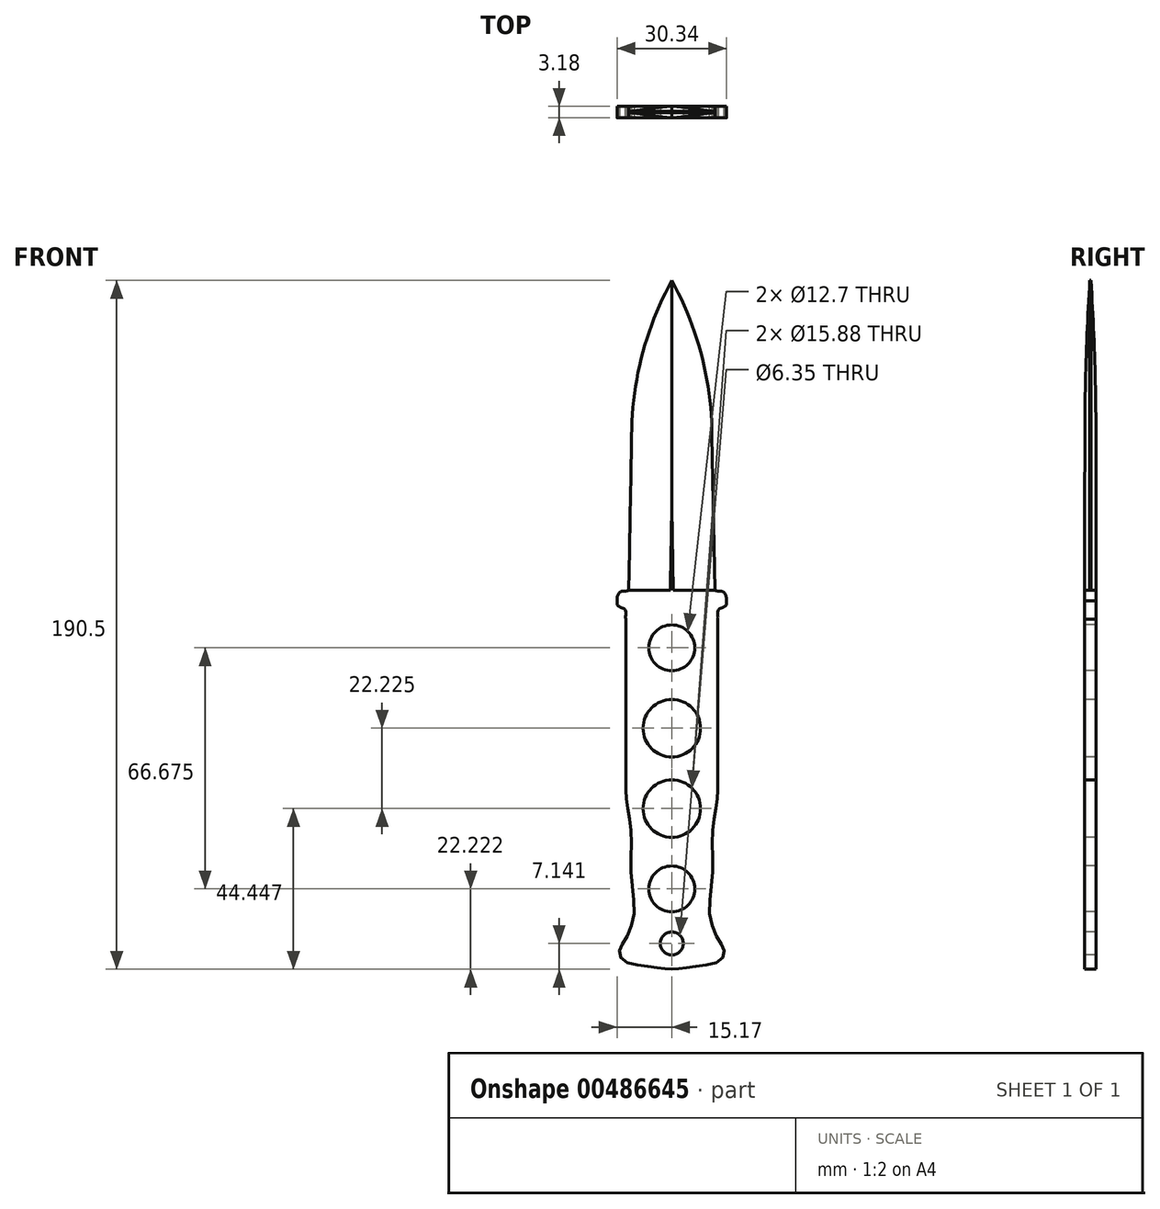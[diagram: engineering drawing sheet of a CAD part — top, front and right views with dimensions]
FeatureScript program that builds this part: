
annotation { "Feature Type Name" : "Feature", "Feature Type Description" : "" }
export const myFeature = defineFeature(function(context is Context, id is Id, definition is map)
    precondition{}
    {
        {
            var Q0;
            Q0=qCreatedBy(makeId("Front.planeOp"),FACE);
            var sketch = newSketch(context, id + "F0", { "sketchPlane" : qUnion([Q0])});
            skLineSegment(sketch, "E0", {"start": v(11.9, -41.46) * mm, "end": v(11.11, 1.4) * mm});
            skArc(sketch, "E1", {"start": v(11.11, 1.4) * mm, "mid": v(8.24, 23.53) * mm, "end": v(0, 44.27) * mm});
            skLineSegment(sketch, "E2", {"start": v(-11.9, -41.46) * mm, "end": v(-11.11, 1.4) * mm});
            skArc(sketch, "E3", {"start": v(0, 44.27) * mm, "mid": v(-8.24, 23.53) * mm, "end": v(-11.11, 1.4) * mm});
            skFitSpline(sketch, "E4", {"points": [v(11.9, -41.46) * mm, v(12.83, -41.64) * mm, v(14.42, -41.94) * mm, v(15.12, -43.63) * mm, v(15.12, -44.27) * mm]});
            skFitSpline(sketch, "E5", {"points": [v(-11.9, -41.46) * mm, v(-12.83, -41.64) * mm, v(-14.42, -41.94) * mm, v(-15.12, -43.63) * mm, v(-15.12, -44.27) * mm]});
            skLineSegment(sketch, "E6", {"start": v(15.12, -44.27) * mm, "end": v(-15.12, -44.27) * mm});
            skSolve(sketch);
        }
        {
            var Q0;
            Q0=makeQuery(id+"F0.imprint","IMPRINT",FACE,{"disambiguationData":[TD([[makeQuery(id+"F0.imprint","IMPRINT",EDGE,{"derivedFrom":sQuery(id+"F0.wireOp",EDGE,"E0")}),1.0]])]});
            extrude(context, id + "F1", {"entities" : qUnion([Q0]), "depth" : 3.17 * mm});
        }
        {
            var Q0;
            Q0=makeQuery(id+"F1.opExtrude","SWEPT_FACE",FACE,{"disambiguationData":[OSD([sQuery(id+"F0.wireOp",EDGE,"E6")])]});
            cPlane(context, id + "F2", {"entities" : qUnion([Q0]), "cplaneType" : CPlaneType.OFFSET, "offset" : 3.45 * mm, "oppositeDirection" : true, "width" : 152.4 * mm, "height" : 152.4 * mm});
        }
        {
            var Q0;
            Q0=makeQuery(id+"F1.opExtrude","CAP_FACE",FACE,{"disambiguationData":[OSD([sQuery(id+"F0.wireOp",EDGE,"E0"),sQuery(id+"F0.wireOp",EDGE,"E1"),sQuery(id+"F0.wireOp",EDGE,"E2"),sQuery(id+"F0.wireOp",EDGE,"E3"),sQuery(id+"F0.wireOp",EDGE,"E4"),sQuery(id+"F0.wireOp",EDGE,"E5"),sQuery(id+"F0.wireOp",EDGE,"E6")])],"isStart":false});
            cPlane(context, id + "F3", {"entities" : qUnion([Q0]), "cplaneType" : CPlaneType.OFFSET, "offset" : 1.59 * mm, "oppositeDirection" : true, "width" : 152.4 * mm, "height" : 152.4 * mm});
        }
        {
            var Q0;
            Q0=qCreatedBy(id+"F3.planeOp",FACE);
            var sketch = newSketch(context, id + "F4", { "sketchPlane" : qUnion([Q0])});
            skLineSegment(sketch, "E7", {"start": v(11.9, -41.46) * mm, "end": v(11.11, 1.4) * mm});
            skArc(sketch, "E8", {"start": v(11.11, 1.4) * mm, "mid": v(8.24, 23.53) * mm, "end": v(0, 44.27) * mm});
            skLineSegment(sketch, "E9", {"start": v(-11.9, -41.46) * mm, "end": v(-11.11, 1.4) * mm});
            skArc(sketch, "E10", {"start": v(0, 44.27) * mm, "mid": v(-8.24, 23.53) * mm, "end": v(-11.11, 1.4) * mm});
            skFitSpline(sketch, "E11", {"points": [v(11.9, -41.46) * mm, v(12.83, -41.64) * mm, v(14.42, -41.94) * mm, v(15.12, -43.63) * mm, v(15.12, -44.27) * mm]});
            skFitSpline(sketch, "E12", {"points": [v(-11.9, -41.46) * mm, v(-12.83, -41.64) * mm, v(-14.42, -41.94) * mm, v(-15.12, -43.63) * mm, v(-15.12, -44.27) * mm]});
            skLineSegment(sketch, "E13", {"start": v(15.12, -44.27) * mm, "end": v(-15.12, -44.27) * mm});
            skSolve(sketch);
        }
        {
            var Q0;
            Q0=makeQuery(id+"F1.opExtrude","CAP_FACE",FACE,{"disambiguationData":[OSD([sQuery(id+"F0.wireOp",EDGE,"E0"),sQuery(id+"F0.wireOp",EDGE,"E1"),sQuery(id+"F0.wireOp",EDGE,"E2"),sQuery(id+"F0.wireOp",EDGE,"E3"),sQuery(id+"F0.wireOp",EDGE,"E4"),sQuery(id+"F0.wireOp",EDGE,"E5"),sQuery(id+"F0.wireOp",EDGE,"E6")])],"isStart":true});
            var sketch = newSketch(context, id + "F5", { "sketchPlane" : qUnion([Q0])});
            skLineSegment(sketch, "E14", {"start": v(0, -44.27) * mm, "end": v(0, 44.27) * mm});
            skSolve(sketch);
        }
        {
            var Q0;
            Q0=makeQuery(id+"F1.opExtrude","CAP_FACE",FACE,{"disambiguationData":[OSD([sQuery(id+"F0.wireOp",EDGE,"E0"),sQuery(id+"F0.wireOp",EDGE,"E1"),sQuery(id+"F0.wireOp",EDGE,"E2"),sQuery(id+"F0.wireOp",EDGE,"E3"),sQuery(id+"F0.wireOp",EDGE,"E4"),sQuery(id+"F0.wireOp",EDGE,"E5"),sQuery(id+"F0.wireOp",EDGE,"E6")])],"isStart":false});
            var sketch = newSketch(context, id + "F6", { "sketchPlane" : qUnion([Q0])});
            skLineSegment(sketch, "E15", {"start": v(0, -44.27) * mm, "end": v(0, 44.27) * mm});
            skSolve(sketch);
        }
        {
            var Q0;
            Q0=qCreatedBy(id+"F2.planeOp",FACE);
            var sketch = newSketch(context, id + "F7", { "sketchPlane" : qUnion([Q0])});
            skLineSegment(sketch, "E16", {"start": v(0, 3.23) * mm, "end": v(13.2, 1.59) * mm});
            skLineSegment(sketch, "E17", {"start": v(13.2, 1.59) * mm, "end": v(0, -0.05) * mm});
            skLineSegment(sketch, "E18", {"start": v(0, -0.05) * mm, "end": v(13.2, -0.05) * mm});
            skLineSegment(sketch, "E19", {"start": v(13.2, -0.05) * mm, "end": v(13.2, 1.59) * mm});
            skLineSegment(sketch, "E20", {"start": v(0, 3.23) * mm, "end": v(13.2, 3.23) * mm});
            skLineSegment(sketch, "E21", {"start": v(13.2, 3.23) * mm, "end": v(13.2, 1.59) * mm});
            skSolve(sketch);
        }
        {
            var Q0;
            Q0 = qSketchRegion(id + "F7", true);
            var Q1;
            Q1=sQuery(id+"F4.wireOp",EDGE,"E7");
            var Q2;
            Q2=sQuery(id+"F4.wireOp",EDGE,"E8");
            sweep(context, id + "F8", {"operationType" : NewBodyOperationType.REMOVE, "profiles" : qUnion([Q0]), "path" : qUnion([Q1, Q2])});
        }
        {
            var Q0;
            Q0=qCreatedBy(id+"F2.planeOp",FACE);
            var sketch = newSketch(context, id + "F9", { "sketchPlane" : qUnion([Q0])});
            skLineSegment(sketch, "E22", {"start": v(0, 3.23) * mm, "end": v(-13.2, 1.59) * mm});
            skLineSegment(sketch, "E23", {"start": v(-13.2, 1.59) * mm, "end": v(-13.2, 3.23) * mm});
            skLineSegment(sketch, "E24", {"start": v(-13.2, 3.23) * mm, "end": v(0, 3.23) * mm});
            skLineSegment(sketch, "E25", {"start": v(-13.2, 1.59) * mm, "end": v(0, -0.05) * mm});
            skLineSegment(sketch, "E26", {"start": v(0, -0.05) * mm, "end": v(-13.2, -0.05) * mm});
            skLineSegment(sketch, "E27", {"start": v(-13.2, -0.05) * mm, "end": v(-13.2, 1.59) * mm});
            skSolve(sketch);
        }
        {
            var Q0;
            Q0 = qSketchRegion(id + "F9", true);
            var Q1;
            Q1=sQuery(id+"F4.wireOp",EDGE,"E9");
            var Q2;
            Q2=sQuery(id+"F4.wireOp",EDGE,"E10");
            sweep(context, id + "F10", {"operationType" : NewBodyOperationType.REMOVE, "profiles" : qUnion([Q0]), "path" : qUnion([Q1, Q2])});
        }
        {
            var Q0;
            Q0=qCreatedBy(makeId("Front.planeOp"),FACE);
            var sketch = newSketch(context, id + "F11", { "sketchPlane" : qUnion([Q0])});
            skLineSegment(sketch, "E28", {"start": v(12.7, -49.4) * mm, "end": v(12.7, -93.84) * mm});
            skFitSpline(sketch, "E29", {"points": [v(0, -146.23) * mm, v(3.02, -145.87) * mm, v(7.7, -145.3) * mm, v(13.31, -143.82) * mm, v(14.5, -141.27) * mm, v(13.04, -138.32) * mm, v(10.51, -131.36) * mm, v(11.22, -120.49) * mm, v(11.2, -109.32) * mm, v(12.14, -101.91) * mm, v(12.7, -96.98) * mm, v(12.7, -94.89) * mm, v(12.7, -93.84) * mm]});
            skLineSegment(sketch, "E30", {"start": v(-12.7, -49.4) * mm, "end": v(-12.7, -93.84) * mm});
            skFitSpline(sketch, "E31", {"points": [v(0, -146.23) * mm, v(-3.02, -145.87) * mm, v(-7.7, -145.3) * mm, v(-13.31, -143.82) * mm, v(-14.5, -141.27) * mm, v(-13.04, -138.32) * mm, v(-10.51, -131.36) * mm, v(-11.22, -120.49) * mm, v(-11.2, -109.32) * mm, v(-12.14, -101.91) * mm, v(-12.7, -96.98) * mm, v(-12.7, -94.89) * mm, v(-12.7, -93.84) * mm]});
            skFitSpline(sketch, "E32", {"points": [v(15.12, -44.27) * mm, v(15.12, -44.4) * mm, v(15, -45.59) * mm, v(12.94, -46.8) * mm, v(12.77, -48.66) * mm, v(12.7, -49.4) * mm]});
            skFitSpline(sketch, "E33", {"points": [v(-15.12, -44.27) * mm, v(-15.12, -44.4) * mm, v(-15, -45.59) * mm, v(-12.94, -46.8) * mm, v(-12.77, -48.66) * mm, v(-12.7, -49.4) * mm]});
            skLineSegment(sketch, "E34", {"start": v(15.12, -44.27) * mm, "end": v(-15.12, -44.27) * mm});
            skSolve(sketch);
        }
        {
            var Q0;
            Q0 = qSketchRegion(id + "F11", true);
            extrude(context, id + "F12", {"entities" : qUnion([Q0]), "operationType" : NewBodyOperationType.ADD, "depth" : 3.17 * mm});
        }
        {
            var Q0;
            Q0=makeQuery(id+"F12.boolean.opBoolean","MERGE",FACE,{"derivedFrom":[makeQuery(id+"F1.opExtrude","CAP_FACE",FACE,{"disambiguationData":[OSD([sQuery(id+"F0.wireOp",EDGE,"E0"),sQuery(id+"F0.wireOp",EDGE,"E1"),sQuery(id+"F0.wireOp",EDGE,"E2"),sQuery(id+"F0.wireOp",EDGE,"E3"),sQuery(id+"F0.wireOp",EDGE,"E4"),sQuery(id+"F0.wireOp",EDGE,"E5"),sQuery(id+"F0.wireOp",EDGE,"E6")])],"isStart":false}),makeQuery(id+"F12.opExtrude","CAP_FACE",FACE,{"disambiguationData":[OSD([sQuery(id+"F11.wireOp",EDGE,"E28"),sQuery(id+"F11.wireOp",EDGE,"E29"),sQuery(id+"F11.wireOp",EDGE,"E30"),sQuery(id+"F11.wireOp",EDGE,"E31"),sQuery(id+"F11.wireOp",EDGE,"E32"),sQuery(id+"F11.wireOp",EDGE,"E33"),sQuery(id+"F11.wireOp",EDGE,"E34")])],"isStart":false})]});
            var sketch = newSketch(context, id + "F13", { "sketchPlane" : qUnion([Q0])});
            skLineSegment(sketch, "E35", {"start": v(0, -146.23) * mm, "end": v(0, -101.78) * mm});
            skLineSegment(sketch, "E36", {"start": v(0, -101.78) * mm, "end": v(0, -79.56) * mm});
            skLineSegment(sketch, "E37", {"start": v(0, -79.56) * mm, "end": v(0, -57.33) * mm});
            skCircle(sketch, "E38", {"center": v(0, -79.56) * mm, "radius": 7.94 * mm});
            skCircle(sketch, "E39", {"center": v(0, -101.78) * mm, "radius": 7.94 * mm});
            skCircle(sketch, "E40", {"center": v(0, -57.33) * mm, "radius": 6.35 * mm});
            skCircle(sketch, "E41", {"center": v(0, -139.09) * mm, "radius": 3.18 * mm});
            skCircle(sketch, "E42", {"center": v(0, -124) * mm, "radius": 6.35 * mm});
            skSolve(sketch);
        }
        {
            var Q0;
            Q0 = qSketchRegion(id + "F13", true);
            extrude(context, id + "F14", {"entities" : qUnion([Q0]), "operationType" : NewBodyOperationType.REMOVE, "endBound" : BoundingType.UP_TO_NEXT, "oppositeDirection" : true, "depth" : 25.4 * mm});
        }
    });
